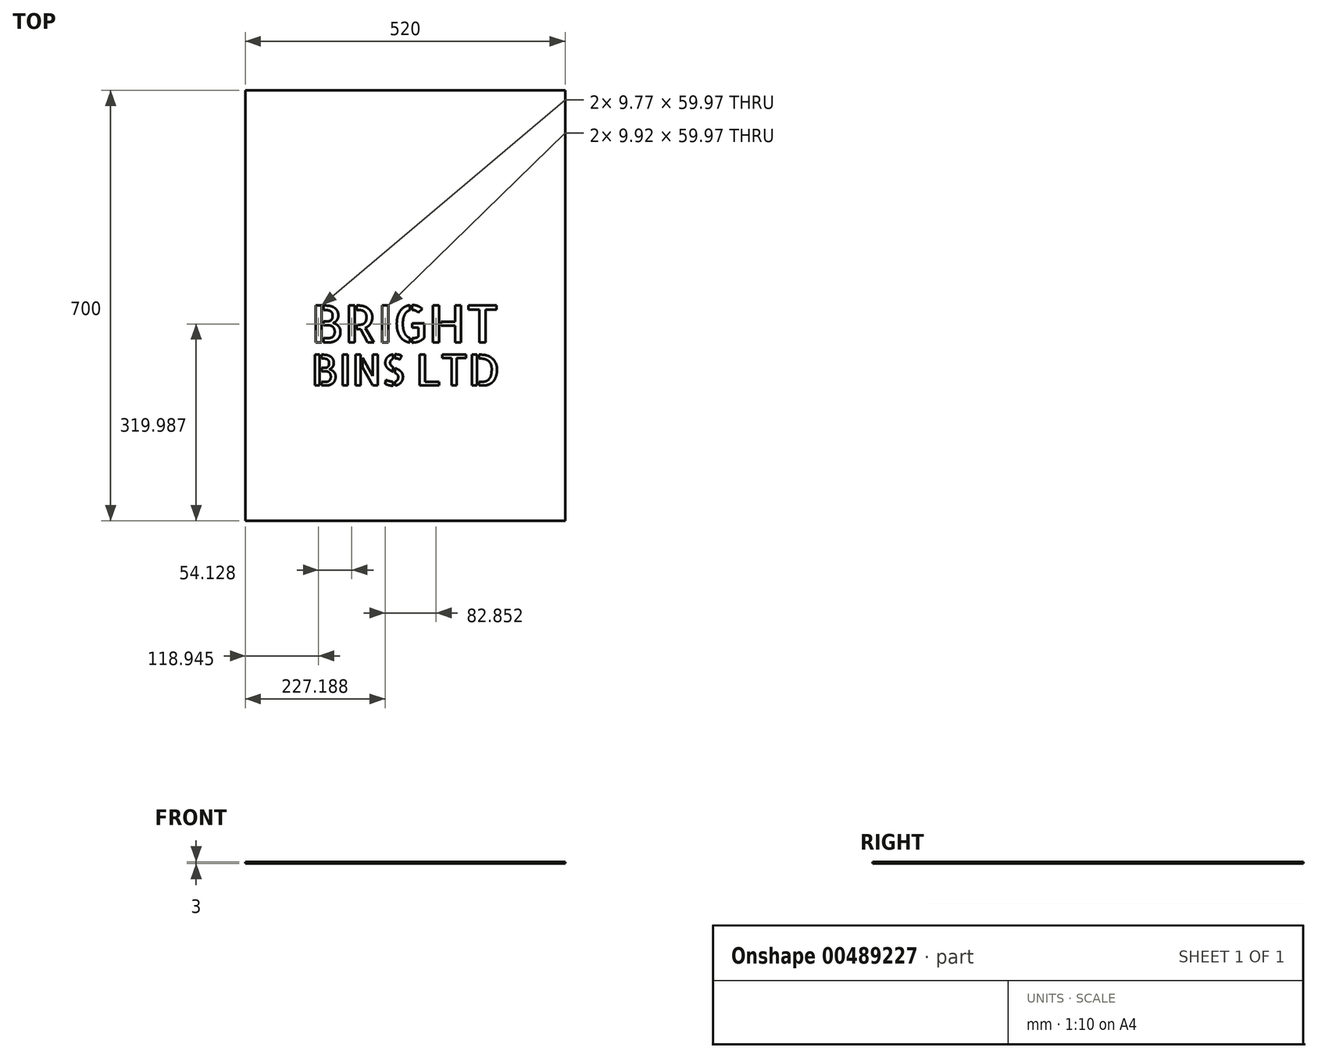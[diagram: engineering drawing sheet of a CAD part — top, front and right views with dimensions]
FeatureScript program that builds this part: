
annotation { "Feature Type Name" : "Feature", "Feature Type Description" : "" }
export const myFeature = defineFeature(function(context is Context, id is Id, definition is map)
    precondition{}
    {
        {
            var Q0;
            Q0=qCreatedBy(makeId("Top.planeOp"),FACE);
            var sketch = newSketch(context, id + "F0", { "sketchPlane" : qUnion([Q0])});
            skLineSegment(sketch, "E0.bottom", {"start": v(-366.95, -131.04) * mm, "end": v(153.05, -131.04) * mm});
            skLineSegment(sketch, "E0.top", {"start": v(-366.95, -831.04) * mm, "end": v(153.05, -831.04) * mm});
            skLineSegment(sketch, "E0.left", {"start": v(-366.95, -131.04) * mm, "end": v(-366.95, -831.04) * mm});
            skLineSegment(sketch, "E0.right", {"start": v(153.05, -131.04) * mm, "end": v(153.05, -831.04) * mm});
            skText(sketch, "E1", { "text": "BRIGHT", "fontName": "AllertaStencil-Regular.ttf"});
            skText(sketch, "E2", { "text": "BINS LTD\n", "fontName": "AllertaStencil-Regular.ttf"});
            const initialGuessF0  = {"E1": [-0.2607, -0.54104, 1, 0, 0.06], "E2": [-0.2607, -0.61123, 1, 0, 0.05018]};
            skSetInitialGuess(sketch, initialGuessF0);
            skSolve(sketch);
        }
        {
            var Q0;
            Q0 = qSketchRegion(id + "F0", true);
            extrude(context, id + "F1", {"entities" : qUnion([Q0]), "depth" : 3 * mm});
        }
    });
